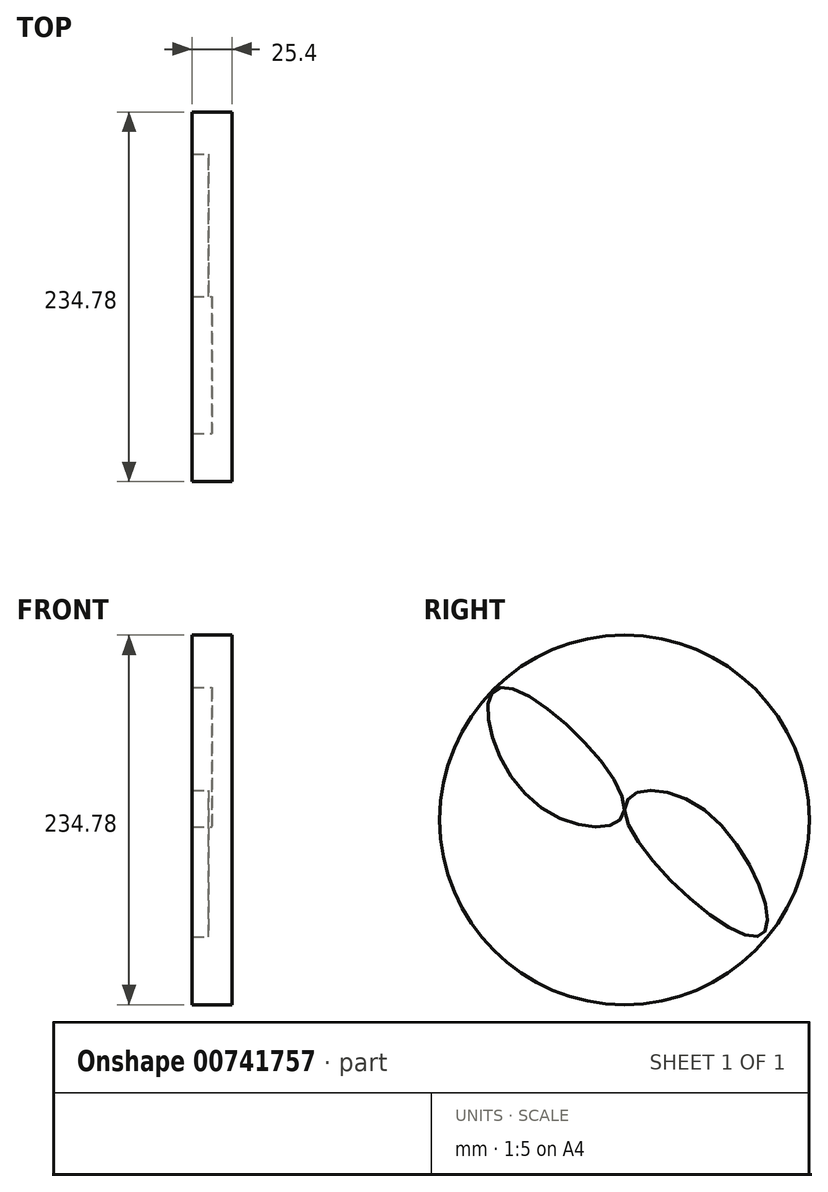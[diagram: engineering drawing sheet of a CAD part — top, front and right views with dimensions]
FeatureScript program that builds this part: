
annotation { "Feature Type Name" : "Feature", "Feature Type Description" : "" }
export const myFeature = defineFeature(function(context is Context, id is Id, definition is map)
    precondition{}
    {
        {
            var Q0;
            Q0=qCreatedBy(makeId("Right.planeOp"),FACE);
            var sketch = newSketch(context, id + "F0", { "sketchPlane" : qUnion([Q0])});
            skCircle(sketch, "E0", {"center": v(0, -6.24) * mm, "radius": 117.39 * mm});
            skSolve(sketch);
        }
        {
            var Q0;
            Q0=sQuery(id+"F0.wireOp",EDGE,"E0");
            extrude(context, id + "F1", {"bodyType" : ToolBodyType.SURFACE, "surfaceEntities" : qUnion([Q0]), "depth" : 25.4 * mm, "offsetDistance" : 25.4 * mm});
        }
        {
            var Q0;
            Q0=qCreatedBy(makeId("Right.planeOp"),FACE);
            var sketch = newSketch(context, id + "F2", { "sketchPlane" : qUnion([Q0])});
            skFitSpline(sketch, "E1", {"points": [v(0, 0) * mm, v(85.31, -80.23) * mm, v(50.62, 0) * mm, v(0, 0) * mm]});
            skSolve(sketch);
        }
        {
            var Q0;
            Q0=sQuery(id+"F2.wireOp",EDGE,"E1");
            extrude(context, id + "F3", {"bodyType" : ToolBodyType.SURFACE, "surfaceEntities" : qUnion([Q0]), "depth" : 10.4 * mm, "offsetDistance" : 25.4 * mm});
        }
        {
            var Q0;
            Q0=qCreatedBy(makeId("Right.planeOp"),FACE);
            var sketch = newSketch(context, id + "F4", { "sketchPlane" : qUnion([Q0])});
            skFitSpline(sketch, "E2", {"points": [v(0, 0) * mm, v(-79.04, 77.77) * mm, v(-59.57, 6.84) * mm, v(0, 0) * mm]});
            skSolve(sketch);
        }
        {
            var Q0;
            Q0=sQuery(id+"F4.wireOp",EDGE,"E2");
            extrude(context, id + "F5", {"bodyType" : ToolBodyType.SURFACE, "surfaceEntities" : qUnion([Q0]), "depth" : 12.7 * mm, "offsetDistance" : 25.4 * mm});
        }
    });
